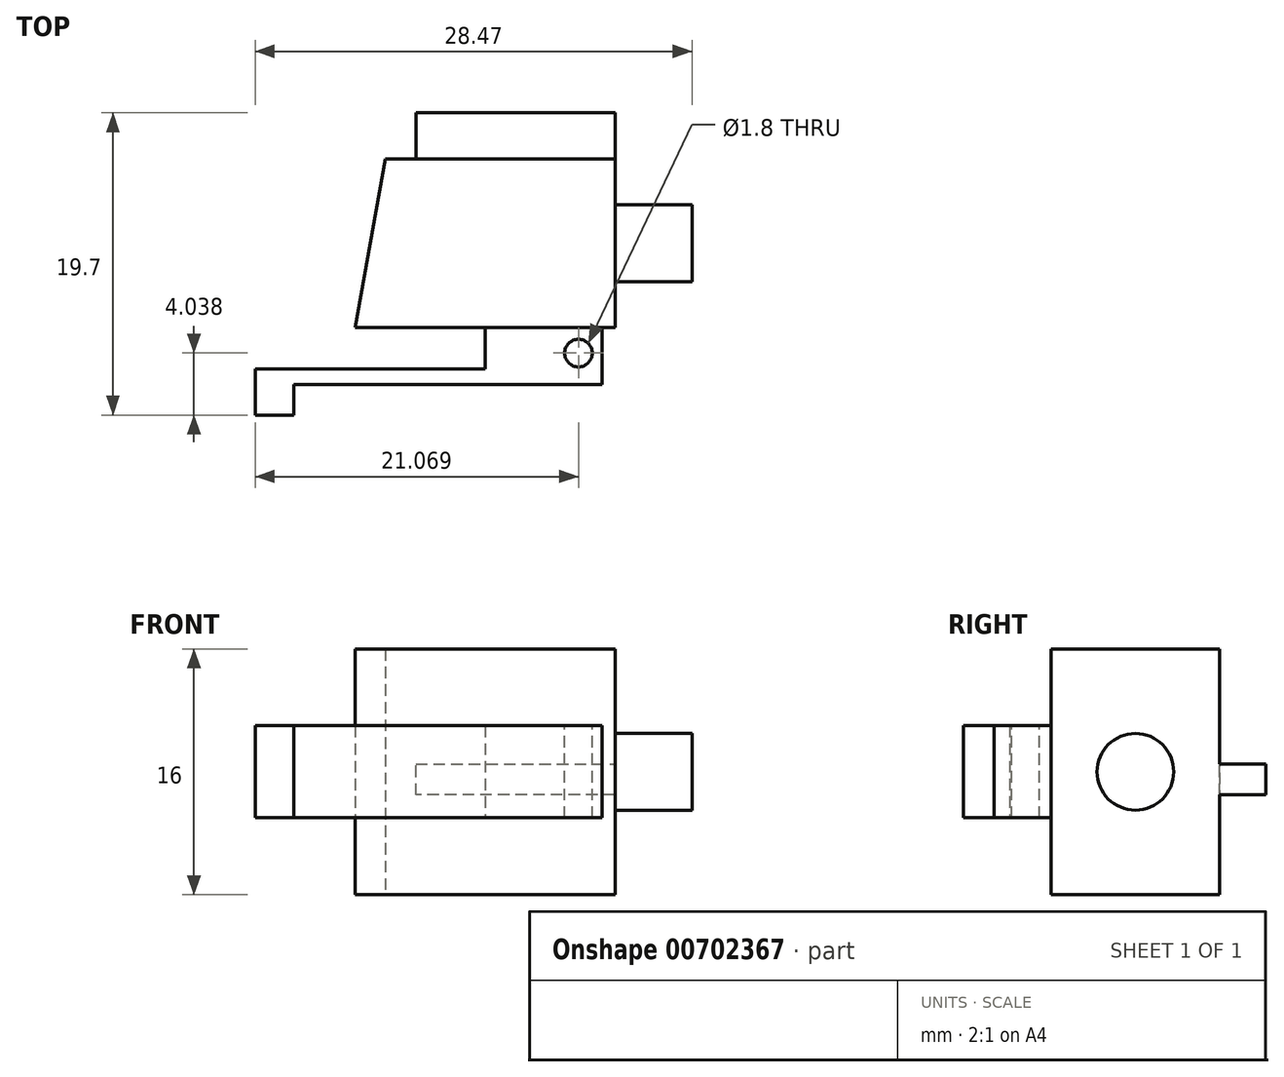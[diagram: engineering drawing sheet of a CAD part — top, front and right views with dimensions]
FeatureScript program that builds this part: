
annotation { "Feature Type Name" : "Feature", "Feature Type Description" : "" }
export const myFeature = defineFeature(function(context is Context, id is Id, definition is map)
    precondition{}
    {
        {
            var Q0;
            Q0=qCreatedBy(makeId("Top.planeOp"),FACE);
            var sketch = newSketch(context, id + "F0", { "sketchPlane" : qUnion([Q0])});
            skLineSegment(sketch, "E0.bottom", {"start": v(-17.57, 7.65) * mm, "end": v(-2.57, 7.65) * mm});
            skLineSegment(sketch, "E0.top", {"start": v(-19.51, -3.35) * mm, "end": v(-2.57, -3.35) * mm});
            skLineSegment(sketch, "E0.left", {"start": v(-17.57, 7.65) * mm, "end": v(-19.51, -3.35) * mm});
            skLineSegment(sketch, "E0.right", {"start": v(-2.57, 7.65) * mm, "end": v(-2.57, -3.35) * mm});
            skSolve(sketch);
        }
        {
            var Q0;
            Q0=makeQuery(id+"F0.imprint","IMPRINT",FACE,{"disambiguationData":[TD([[makeQuery(id+"F0.imprint","IMPRINT",EDGE,{"derivedFrom":sQuery(id+"F0.wireOp",EDGE,"E0.bottom")}),-1.0]])]});
            extrude(context, id + "F1", {"entities" : qUnion([Q0]), "depth" : 18 * mm, "offsetDistance" : 25 * mm});
        }
        {
            var Q0;
            Q0=makeQuery(id+"F1.opExtrude","SWEPT_FACE",FACE,{"disambiguationData":[OSD([sQuery(id+"F0.wireOp",EDGE,"E0.right")])]});
            var sketch = newSketch(context, id + "F2", { "sketchPlane" : qUnion([Q0])});
            skLineSegment(sketch, "E1", {"start": v(7.65, 18) * mm, "end": v(-3.35, 0) * mm, "construction": true});
            skLineSegment(sketch, "E2", {"start": v(-3.35, 18) * mm, "end": v(7.65, 0) * mm, "construction": true});
            skCircle(sketch, "E3", {"center": v(2.15, 9) * mm, "radius": 2.5 * mm});
            skSolve(sketch);
        }
        {
            var Q0;
            Q0=makeQuery(id+"F2.imprint","IMPRINT",FACE,{"disambiguationData":[TD([[makeQuery(id+"F2.imprint","IMPRINT",EDGE,{"derivedFrom":sQuery(id+"F2.wireOp",EDGE,"E3")}),1.0]])]});
            extrude(context, id + "F3", {"entities" : qUnion([Q0]), "operationType" : NewBodyOperationType.ADD, "depth" : 5 * mm, "offsetDistance" : 25 * mm});
        }
        {
            var Q0;
            Q0=makeQuery(id+"F1.opExtrude","SWEPT_FACE",FACE,{"disambiguationData":[OSD([sQuery(id+"F0.wireOp",EDGE,"E0.bottom")])]});
            var sketch = newSketch(context, id + "F4", { "sketchPlane" : qUnion([Q0])});
            skLineSegment(sketch, "E4", {"start": v(12.57, 0) * mm, "end": v(12.57, 7.5) * mm, "construction": true});
            skLineSegment(sketch, "E5", {"start": v(8.28, 0) * mm, "end": v(8.28, 7.5) * mm, "construction": true});
            skLineSegment(sketch, "E6", {"start": v(2.57, 7.5) * mm, "end": v(2.57, 9.5) * mm});
            skLineSegment(sketch, "E7", {"start": v(2.57, 7.5) * mm, "end": v(15.57, 7.5) * mm});
            skLineSegment(sketch, "E8", {"start": v(15.57, 7.5) * mm, "end": v(15.57, 9.5) * mm});
            skLineSegment(sketch, "E9", {"start": v(15.57, 9.5) * mm, "end": v(2.57, 9.5) * mm});
            skSolve(sketch);
        }
        {
            var Q0;
            Q0=makeQuery(id+"F4.imprint","IMPRINT",FACE,{"disambiguationData":[TD([[makeQuery(id+"F4.imprint","IMPRINT",EDGE,{"derivedFrom":sQuery(id+"F4.wireOp",EDGE,"E6")}),1.0]])]});
            extrude(context, id + "F5", {"entities" : qUnion([Q0]), "operationType" : NewBodyOperationType.ADD, "depth" : 3 * mm, "offsetDistance" : 25 * mm});
        }
        {
            var Q0;
            Q0=makeQuery(id+"F1.opExtrude","SWEPT_FACE",FACE,{"disambiguationData":[OSD([sQuery(id+"F0.wireOp",EDGE,"E0.top")])]});
            var sketch = newSketch(context, id + "F6", { "sketchPlane" : qUnion([Q0])});
            skLineSegment(sketch, "E10", {"start": v(-11.04, 0) * mm, "end": v(-11.04, 6) * mm, "construction": true});
            skLineSegment(sketch, "E11", {"start": v(-11.04, 6) * mm, "end": v(-3.45, 6) * mm});
            skLineSegment(sketch, "E12", {"start": v(-3.45, 6) * mm, "end": v(-3.45, 12) * mm});
            skLineSegment(sketch, "E13", {"start": v(-3.45, 12) * mm, "end": v(-11.04, 12) * mm});
            skLineSegment(sketch, "E14", {"start": v(-11.04, 12) * mm, "end": v(-11.04, 6) * mm});
            skSolve(sketch);
        }
        {
            var Q0;
            Q0=makeQuery(id+"F6.imprint","IMPRINT",FACE,{"disambiguationData":[TD([[makeQuery(id+"F6.imprint","IMPRINT",EDGE,{"derivedFrom":sQuery(id+"F6.wireOp",EDGE,"E11")}),1.0]])]});
            extrude(context, id + "F7", {"entities" : qUnion([Q0]), "operationType" : NewBodyOperationType.ADD, "depth" : 3.7 * mm, "offsetDistance" : 25 * mm});
        }
        {
            var Q0;
            Q0=makeQuery(id+"F7.opExtrude","SWEPT_FACE",FACE,{"disambiguationData":[OSD([sQuery(id+"F6.wireOp",EDGE,"E13")])]});
            var sketch = newSketch(context, id + "F8", { "sketchPlane" : qUnion([Q0])});
            skCircle(sketch, "E15", {"center": v(-4.97, -5.01) * mm, "radius": 0.9 * mm});
            skSolve(sketch);
        }
        {
            var Q0;
            Q0=makeQuery(id+"F8.imprint","IMPRINT",FACE,{"disambiguationData":[TD([[makeQuery(id+"F8.imprint","IMPRINT",EDGE,{"derivedFrom":sQuery(id+"F8.wireOp",EDGE,"E15")}),1.0]])]});
            extrude(context, id + "F9", {"entities" : qUnion([Q0]), "operationType" : NewBodyOperationType.REMOVE, "oppositeDirection" : true, "depth" : 10 * mm, "offsetDistance" : 25 * mm});
        }
        {
            var Q0;
            Q0=makeQuery(id+"F7.opExtrude","SWEPT_FACE",FACE,{"disambiguationData":[OSD([sQuery(id+"F6.wireOp",EDGE,"E14")])]});
            var sketch = newSketch(context, id + "F10", { "sketchPlane" : qUnion([Q0])});
            skLineSegment(sketch, "E16", {"start": v(7.05, 12) * mm, "end": v(7.05, 6) * mm});
            skLineSegment(sketch, "E17", {"start": v(7.05, 12) * mm, "end": v(6.05, 12) * mm});
            skLineSegment(sketch, "E18", {"start": v(6.05, 12) * mm, "end": v(6.05, 6) * mm});
            skLineSegment(sketch, "E19", {"start": v(6.05, 6) * mm, "end": v(7.05, 6) * mm});
            skSolve(sketch);
        }
        {
            var Q0;
            Q0=makeQuery(id+"F10.imprint","IMPRINT",FACE,{"disambiguationData":[TD([[makeQuery(id+"F10.imprint","IMPRINT",EDGE,{"derivedFrom":sQuery(id+"F10.wireOp",EDGE,"E16")}),-1.0]])]});
            extrude(context, id + "F11", {"entities" : qUnion([Q0]), "operationType" : NewBodyOperationType.ADD, "depth" : 15 * mm, "offsetDistance" : 25 * mm});
        }
        {
            var Q0;
            Q0=makeQuery(id+"F11.boolean.opBoolean","MERGE",FACE,{"derivedFrom":[makeQuery(id+"F7.opExtrude","CAP_FACE",FACE,{"disambiguationData":[OSD([sQuery(id+"F6.wireOp",EDGE,"E11"),sQuery(id+"F6.wireOp",EDGE,"E12"),sQuery(id+"F6.wireOp",EDGE,"E13"),sQuery(id+"F6.wireOp",EDGE,"E14")])],"isStart":false}),makeQuery(id+"F11.opExtrude","SWEPT_FACE",FACE,{"disambiguationData":[OSD([sQuery(id+"F10.wireOp",EDGE,"E16")])]})]});
            var sketch = newSketch(context, id + "F12", { "sketchPlane" : qUnion([Q0])});
            skLineSegment(sketch, "E20", {"start": v(-26.04, 12) * mm, "end": v(-23.54, 12) * mm});
            skLineSegment(sketch, "E21", {"start": v(-23.54, 12) * mm, "end": v(-23.54, 6) * mm});
            skLineSegment(sketch, "E22", {"start": v(-23.54, 6) * mm, "end": v(-26.04, 6) * mm});
            skLineSegment(sketch, "E23", {"start": v(-26.04, 6) * mm, "end": v(-26.04, 12) * mm});
            skSolve(sketch);
        }
        {
            var Q0;
            Q0=makeQuery(id+"F12.imprint","IMPRINT",FACE,{"disambiguationData":[TD([[makeQuery(id+"F12.imprint","IMPRINT",EDGE,{"derivedFrom":sQuery(id+"F12.wireOp",EDGE,"E20")}),1.0]])]});
            extrude(context, id + "F13", {"entities" : qUnion([Q0]), "operationType" : NewBodyOperationType.ADD, "depth" : 2 * mm, "offsetDistance" : 25 * mm});
        }
        {
            var Q0;
            Q0=makeQuery(id+"F1.opExtrude","CAP_FACE",FACE,{"disambiguationData":[OSD([sQuery(id+"F0.wireOp",EDGE,"E0.bottom"),sQuery(id+"F0.wireOp",EDGE,"E0.top"),sQuery(id+"F0.wireOp",EDGE,"E0.left"),sQuery(id+"F0.wireOp",EDGE,"E0.right")])],"isStart":true});
            extrude(context, id + "F14", {"entities" : qUnion([Q0]), "operationType" : NewBodyOperationType.REMOVE, "oppositeDirection" : true, "depth" : 1 * mm, "offsetDistance" : 25 * mm});
        }
        {
            var Q0;
            Q0=makeQuery(id+"F1.opExtrude","CAP_FACE",FACE,{"disambiguationData":[OSD([sQuery(id+"F0.wireOp",EDGE,"E0.bottom"),sQuery(id+"F0.wireOp",EDGE,"E0.top"),sQuery(id+"F0.wireOp",EDGE,"E0.left"),sQuery(id+"F0.wireOp",EDGE,"E0.right")])],"isStart":false});
            extrude(context, id + "F15", {"entities" : qUnion([Q0]), "operationType" : NewBodyOperationType.REMOVE, "oppositeDirection" : true, "depth" : 1 * mm, "offsetDistance" : 25 * mm});
        }
    });
